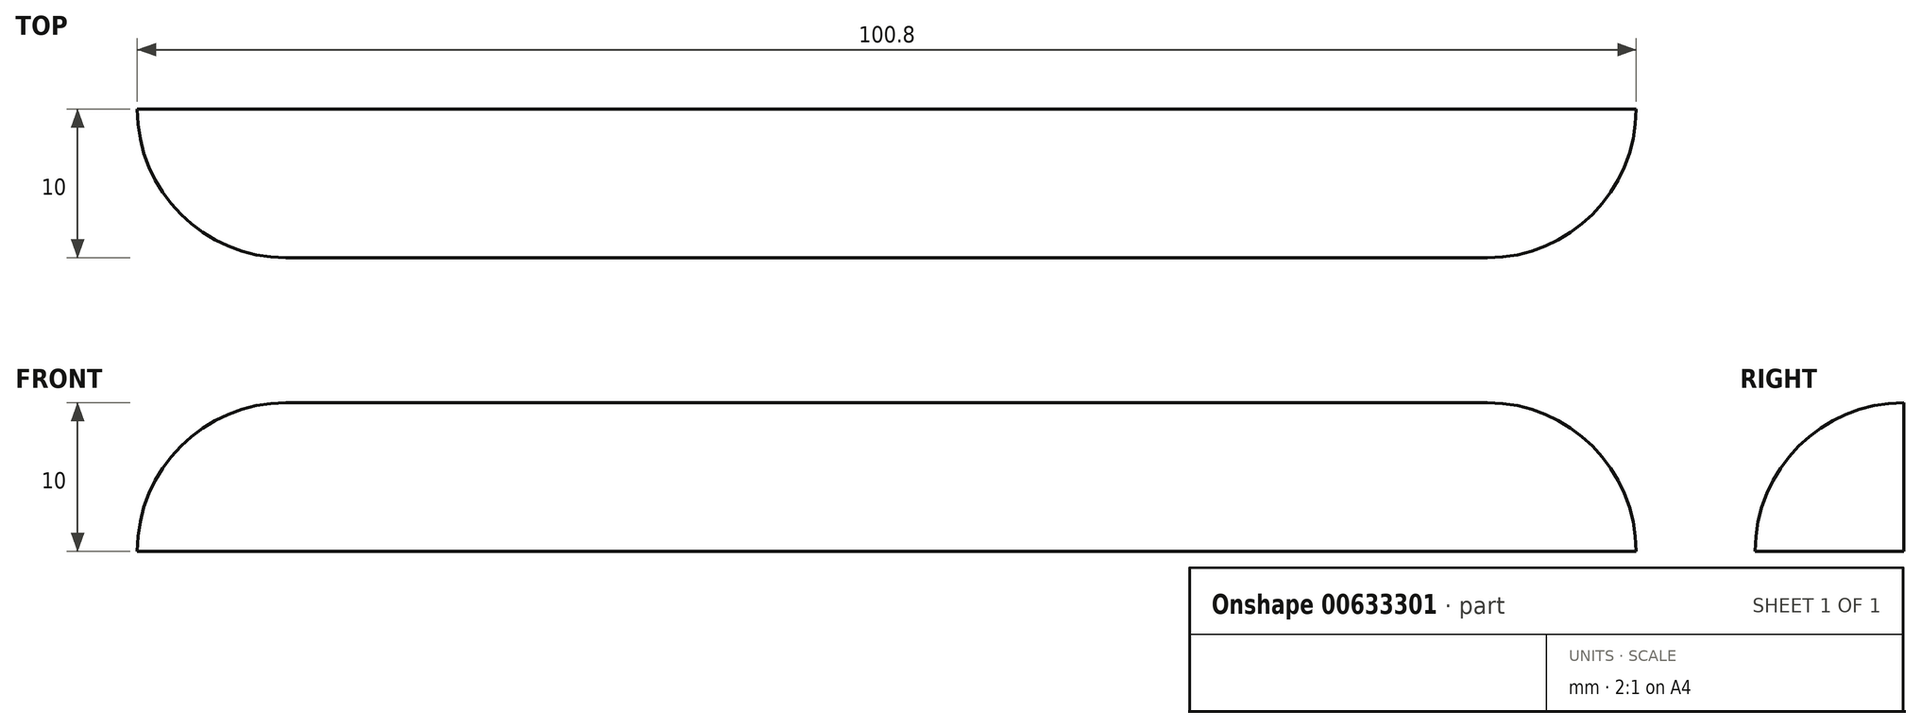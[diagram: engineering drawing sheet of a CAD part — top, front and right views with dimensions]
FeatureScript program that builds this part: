
annotation { "Feature Type Name" : "Feature", "Feature Type Description" : "" }
export const myFeature = defineFeature(function(context is Context, id is Id, definition is map)
    precondition{}
    {
        {
            var Q0;
            Q0=qCreatedBy(makeId("Right.planeOp"),FACE);
            var sketch = newSketch(context, id + "F0", { "sketchPlane" : qUnion([Q0])});
            skLineSegment(sketch, "E0.bottom", {"start": v(5, -5) * mm, "end": v(-5, -5) * mm});
            skLineSegment(sketch, "E0.top", {"start": v(5, 5) * mm, "end": v(5, 5) * mm});
            skLineSegment(sketch, "E0.left", {"start": v(5, -5) * mm, "end": v(5, 5) * mm});
            skLineSegment(sketch, "E0.right", {"start": v(-5, -5) * mm, "end": v(-5, -5) * mm});
            skPoint(sketch, "E0.middle", {"position": v(0, 0) * mm});
            skPoint(sketch, "E1.visualSharp", {"position": v(-5, 5) * mm});
            skArc(sketch, "E1.filletArc", {"start": v(5, 5) * mm, "mid": v(-2.07, 2.07) * mm, "end": v(-5, -5) * mm});
            skSolve(sketch);
        }
        {
            var Q0;
            Q0 = qSketchRegion(id + "F0", true);
            extrude(context, id + "F1", {"entities" : qUnion([Q0]), "endBound" : BoundingType.SYMMETRIC, "depth" : 100.8 * mm, "offsetDistance" : 25 * mm});
        }
        {
            var Q0;
            Q0=makeQuery(id+"F1.opExtrude","CAP_EDGE",EDGE,{"disambiguationData":[OSD([sQuery(id+"F0.wireOp",EDGE,"E1.filletArc")])],"isStart":false});
            var Q1;
            Q1=makeQuery(id+"F1.opExtrude","CAP_EDGE",EDGE,{"disambiguationData":[OSD([sQuery(id+"F0.wireOp",EDGE,"E1.filletArc")])],"isStart":true});
            fillet(context, id + "F2", {"entities" : qUnion([Q0, Q1]), "radius" : 10 * mm, "tangentPropagation" : true, "allowEdgeOverflow" : false});
        }
    });
